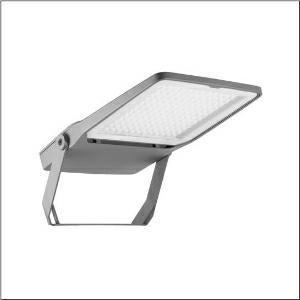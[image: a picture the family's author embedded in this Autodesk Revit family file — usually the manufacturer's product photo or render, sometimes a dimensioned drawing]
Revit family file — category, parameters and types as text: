
# Revit family: floodlight_fl_20_midi___pl43_5xa7682d2a1ac_5ef8
name_source: partatom
category: Lighting Fixtures
units: mm (PartAtom-declared; Revit-internal decimal feet)

## family parameters
Cut with Voids When Loaded = No
Host = Face
Light Source = No
Part Type = Normal
Room Calculation Point = No
Round Connector Dimension = Use Diameter
Shared = No

## types (1)
- --- (1 x LED 4000K / CRI = 70 (unbekannt), 19080 lm, 4000K)
    Apparent Load = 142 VA
    CIE Flux Codes = 32 74 99 100 100
    Color Rendering = 70
    Color Temperature = 4000K
    Default Elevation = 1800 mm
    Description = Floodlight FL 20 midi, floodlight, primary light control with lens, of plastic, primary optical cover: protective disc, of toughened safety glass, transparent, light distribution: PL43, light emission: direct distribution, primary light characteristic: asymmetric, installation type: surface-mounted, LED High Power LED, rated luminous flux: 19.080 lm, light colour: 740, colour temperature: 4000K, control gear: ECG Plus, control: flexible luminous flux parameterisation, time-dependent luminous flux control, digital communication interface, power reduction, overheat protection, electronic power reduction, with terminal, 5-pole, max. 2.5mm², mains connection: 220..240V, AC, 50/60Hz, rated input power: 142W, LED unit, of diecast aluminium, powder-coated, Siteco® metallic grey (DB 702S), length: 654 mm, width: 450 mm, height: 76mm, housing frame, of diecast aluminium, powder-coated, Siteco® metallic grey (DB 702S), mounting bracket, of steel, powder-coated, Siteco® metallic grey (DB 702S), DALIprotection rating (complete): IP66, insulation class (complete): insulation class II (safety insulation), certification: CE, ENEC, VDE, protection symbol: D, permissible ambient temperature for indoor applications: -40..+40°C, permissible ambient temperature for outdoor applications: -40..+50°C, standard: DIN EN 12944, packaging unit: 1 piece

Light Distribution: PL43
    Height = 76 mm
    Lamp = 1 x LED 4000K / CRI >= 70 (unbekannt)
    Lamp Light Flux = 19080 lm
    Lamp count = 1
    Length = 672 mm
    Luminous efficacy = 134 lm/W
    Manufacturer = Siteco
    ModVariant = No
    Model = 5XA7682D2A1AC
    Number of Poles = 1
    OnlyDefault = Yes
    Power Factor = 1
    Product Name = Floodlight FL 20 midi | PL43
    Product group = floodlight | pylon top
    ProductGroupID = 6101
    Protection Class = Protection class II
    Protection Degree = IP 66
    RLX_Detail_Level = 1
    RlxData = <blob elided: 97537 chars, md5=99ba3e74>
    Socket = socket
    Standby Power = 0 W
    System Light Flux = 19080 lm
    System Power = 142 W
    Type Comments = factory setting: luminous flux: 100 % | dim-lin: 254 | 489 mA
    Type Image = l_1005943.jpg
    URL = http://relux.com
    VarID = @adj_143441
    Voltage = 0 V
    Weight = 0.00 kg
    Width = 450 mm

## geometry (parser evidence)
native form markers: Blend x4, Sweep x13
no freeform markers — native parametric forms only
